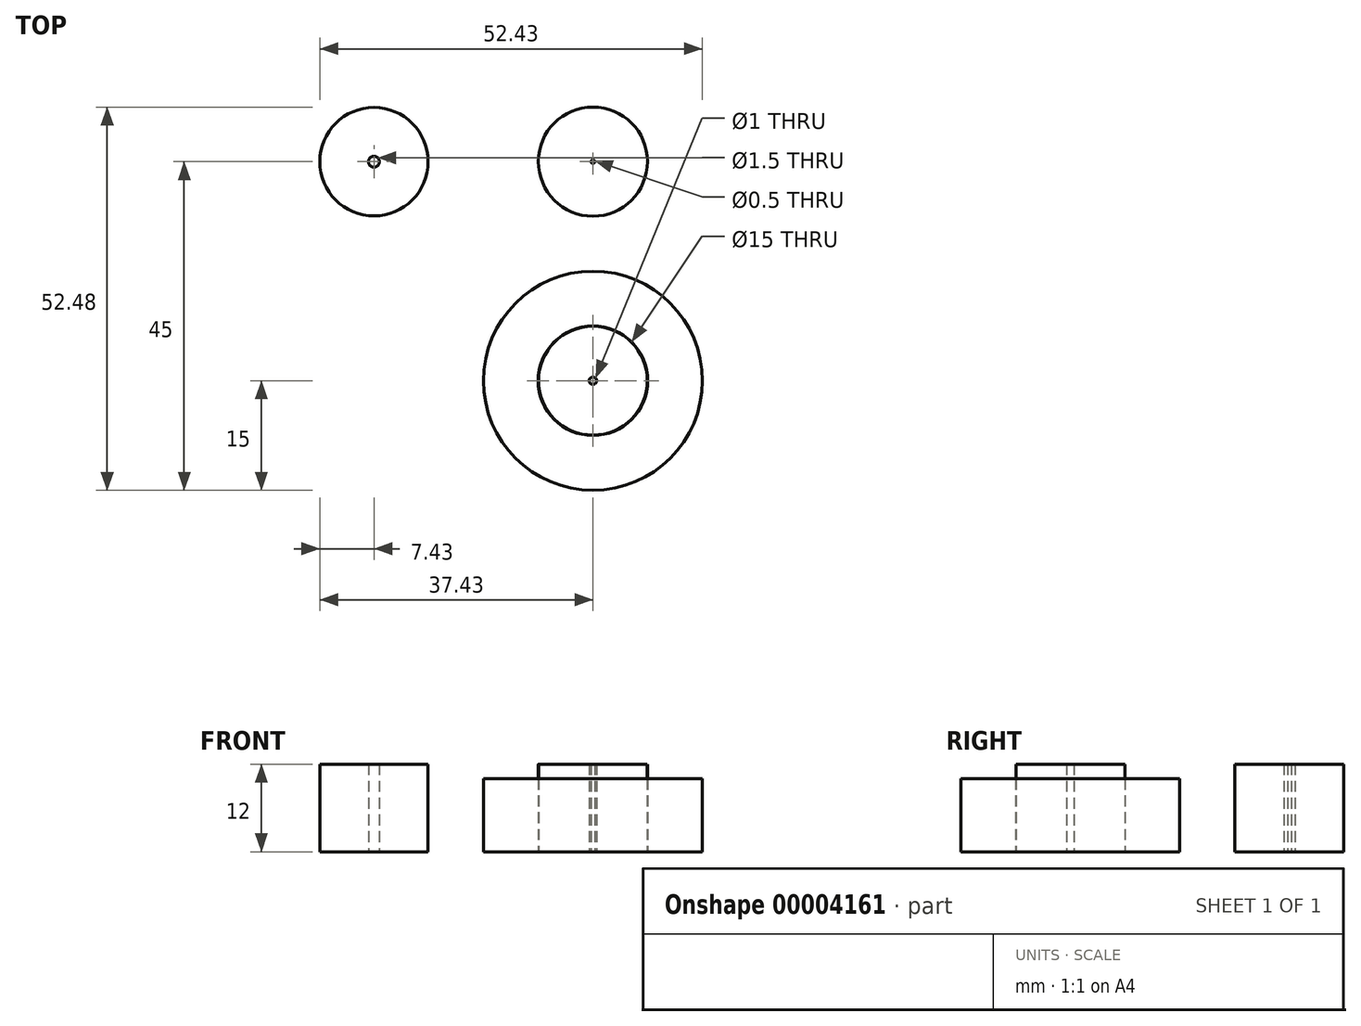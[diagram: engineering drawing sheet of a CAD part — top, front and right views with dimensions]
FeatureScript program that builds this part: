
annotation { "Feature Type Name" : "Feature", "Feature Type Description" : "" }
export const myFeature = defineFeature(function(context is Context, id is Id, definition is map)
    precondition{}
    {
        {
            var Q0;
            Q0=qCreatedBy(makeId("Top.planeOp"),FACE);
            var sketch = newSketch(context, id + "F0", { "sketchPlane" : qUnion([Q0])});
            skCircle(sketch, "E0", {"center": v(0, 0) * mm, "radius": 15 * mm});
            skCircle(sketch, "E1", {"center": v(0, 0) * mm, "radius": 7.5 * mm});
            skSolve(sketch);
        }
        {
            var Q0;
            Q0 = qSketchRegion(id + "F0", true);
            extrude(context, id + "F1", {"entities" : qUnion([Q0]), "depth" : 10 * mm});
        }
        {
            var Q0;
            Q0=qCreatedBy(makeId("Top.planeOp"),FACE);
            var sketch = newSketch(context, id + "F2", { "sketchPlane" : qUnion([Q0])});
            skCircle(sketch, "E2", {"center": v(0, 0) * mm, "radius": 7.45 * mm});
            skCircle(sketch, "E3", {"center": v(0, 30) * mm, "radius": 7.47 * mm});
            skCircle(sketch, "E4", {"center": v(0, 30) * mm, "radius": 0.25 * mm});
            skCircle(sketch, "E5", {"center": v(0, 0) * mm, "radius": 0.5 * mm});
            skCircle(sketch, "E6", {"center": v(-30, 30) * mm, "radius": 7.42 * mm});
            skCircle(sketch, "E7", {"center": v(-30, 30) * mm, "radius": 0.75 * mm});
            skSolve(sketch);
        }
        {
            var Q0;
            Q0 = qSketchRegion(id + "F2", true);
            extrude(context, id + "F3", {"entities" : qUnion([Q0]), "depth" : 12 * mm});
        }
    });
